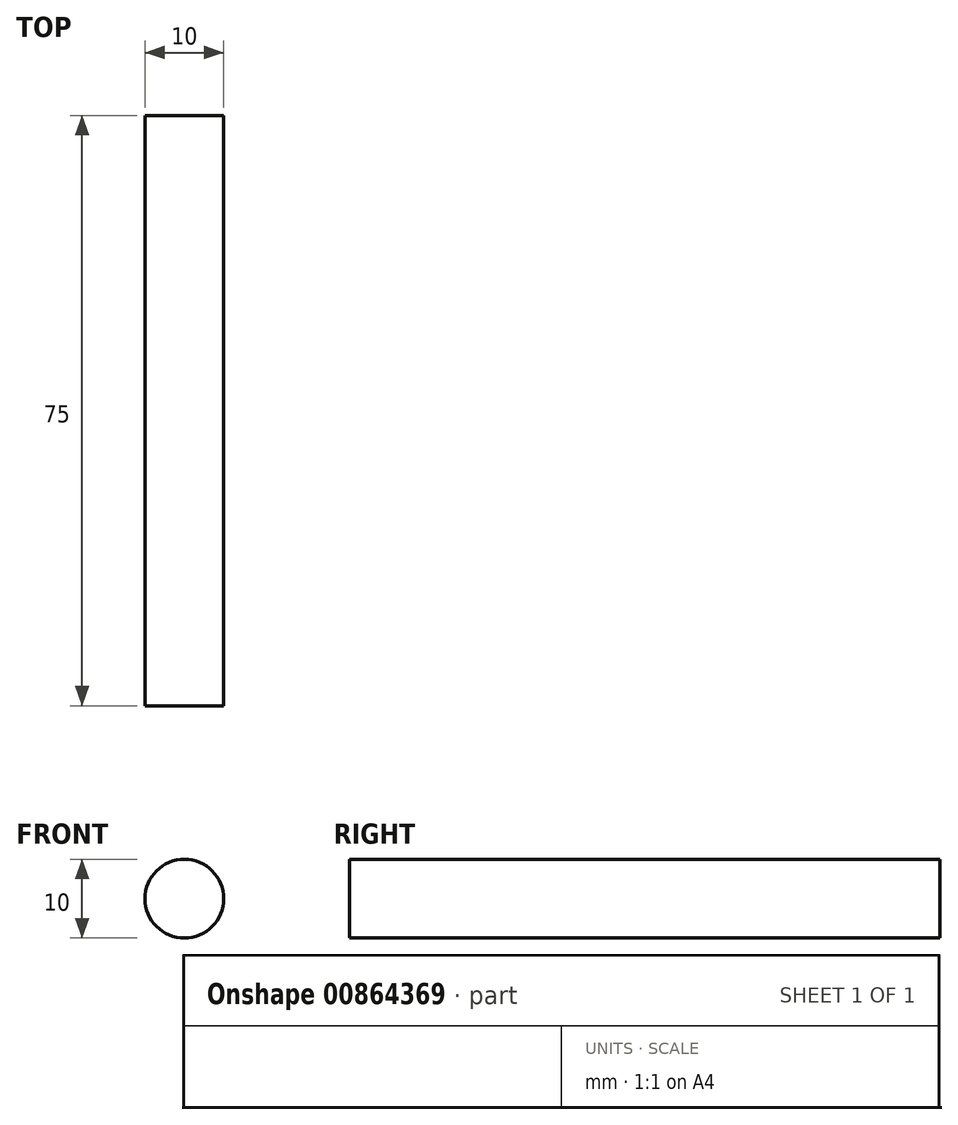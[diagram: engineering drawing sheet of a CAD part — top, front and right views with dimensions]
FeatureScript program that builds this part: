
annotation { "Feature Type Name" : "Feature", "Feature Type Description" : "" }
export const myFeature = defineFeature(function(context is Context, id is Id, definition is map)
    precondition{}
    {
        {
            var Q0;
            Q0=qCreatedBy(makeId("Front.planeOp"),FACE);
            var sketch = newSketch(context, id + "F0", { "sketchPlane" : qUnion([Q0])});
            skCircle(sketch, "E0", {"center": v(0, 0) * mm, "radius": 5 * mm});
            skSolve(sketch);
        }
        {
            var Q0;
            Q0=makeQuery(id+"F0.imprint","IMPRINT",FACE,{"disambiguationData":[TD([[makeQuery(id+"F0.imprint","IMPRINT",EDGE,{"derivedFrom":sQuery(id+"F0.wireOp",EDGE,"E0")}),1.0]])]});
            extrude(context, id + "F1", {"entities" : qUnion([Q0]), "depth" : 75 * mm, "offsetDistance" : 25 * mm});
        }
    });
